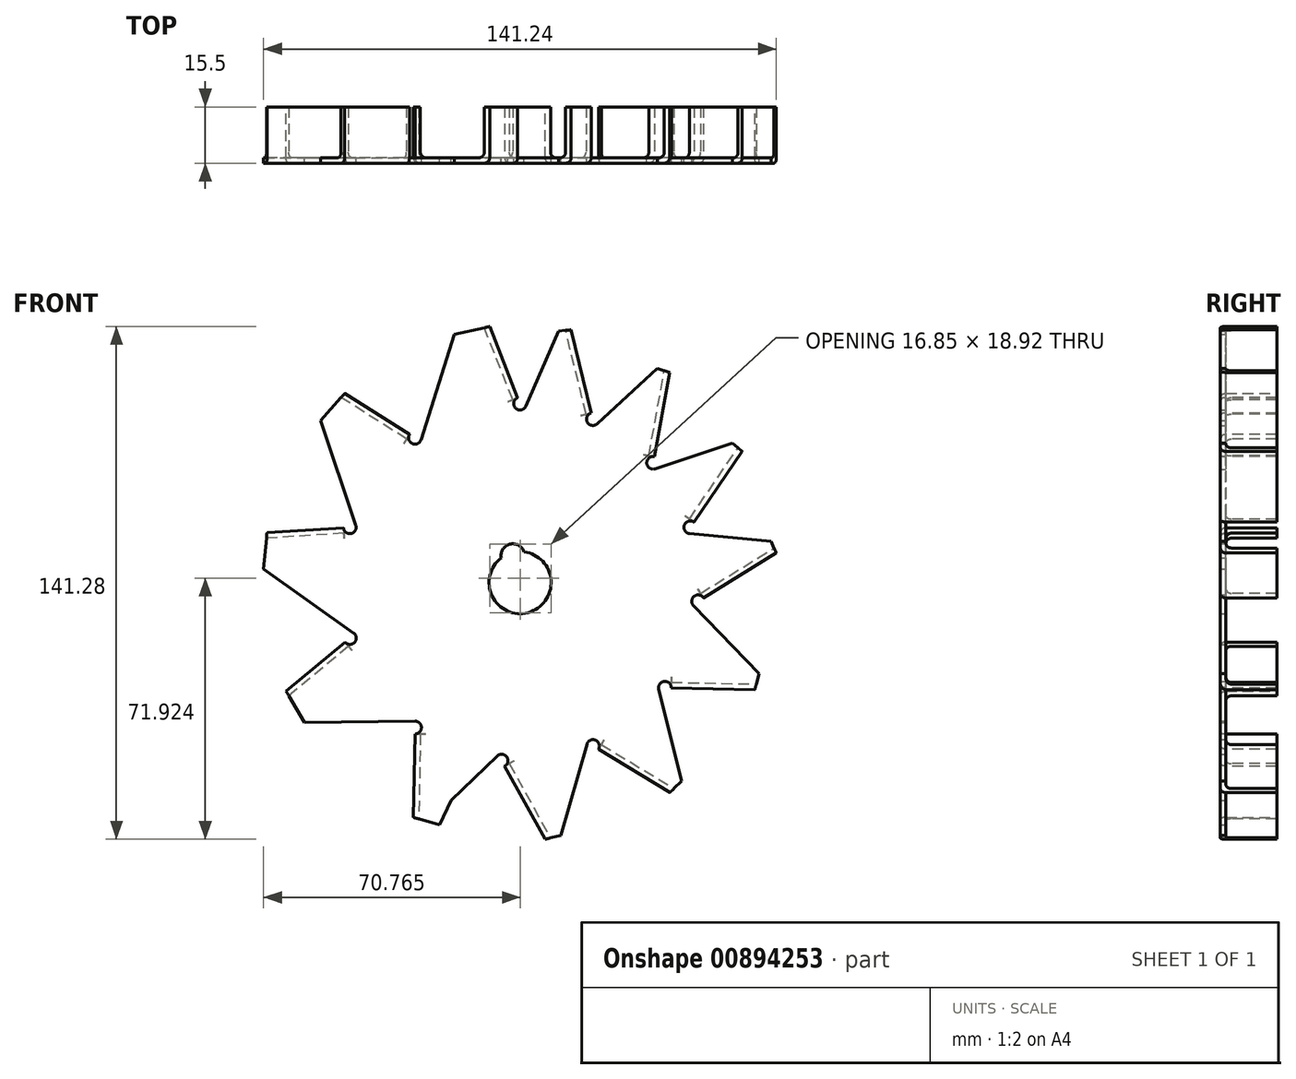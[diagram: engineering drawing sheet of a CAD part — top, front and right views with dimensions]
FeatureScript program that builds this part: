
annotation { "Feature Type Name" : "Feature", "Feature Type Description" : "" }
export const myFeature = defineFeature(function(context is Context, id is Id, definition is map)
    precondition{}
    {
        {
            var Q0;
            Q0=qCreatedBy(makeId("Front.planeOp"),FACE);
            var sketch = newSketch(context, id + "F0", { "sketchPlane" : qUnion([Q0])});
            skArc(sketch, "E0", {"start": v(-5.18, 6.8) * mm, "mid": v(2.21, -8.26) * mm, "end": v(1.09, 8.48) * mm});
            skArc(sketch, "E1", {"start": v(-0.64, 50.93) * mm, "mid": v(-1.26, 48.08) * mm, "end": v(1.6, 48.6) * mm});
            skArc(sketch, "E2", {"start": v(19.64, 46.74) * mm, "mid": v(18.5, 44.21) * mm, "end": v(21.23, 43.75) * mm});
            skArc(sketch, "E3", {"start": v(36.95, 34.71) * mm, "mid": v(34.9, 32.86) * mm, "end": v(37.2, 31.33) * mm});
            skArc(sketch, "E4", {"start": v(47.87, 16.68) * mm, "mid": v(45.24, 15.83) * mm, "end": v(46.72, 13.5) * mm});
            skArc(sketch, "E5", {"start": v(50.52, -4.23) * mm, "mid": v(47.96, -3.77) * mm, "end": v(47.77, -6.37) * mm});
            skArc(sketch, "E6", {"start": v(41.65, -29) * mm, "mid": v(39.7, -27.22) * mm, "end": v(38.2, -29.39) * mm});
            skArc(sketch, "E7", {"start": v(21.59, -45.93) * mm, "mid": v(20.79, -43.42) * mm, "end": v(18.4, -44.54) * mm});
            skArc(sketch, "E8", {"start": v(-4.25, -50.57) * mm, "mid": v(-3.69, -48) * mm, "end": v(-6.3, -47.78) * mm});
            skArc(sketch, "E9", {"start": v(-28.95, -41.68) * mm, "mid": v(-27.16, -39.94) * mm, "end": v(-28.93, -38.18) * mm});
            skArc(sketch, "E10", {"start": v(-48.22, -16.4) * mm, "mid": v(-45.59, -16.47) * mm, "end": v(-45.86, -13.86) * mm});
            skArc(sketch, "E11", {"start": v(-48.64, 15.1) * mm, "mid": v(-46.56, 13.5) * mm, "end": v(-45.23, 15.77) * mm});
            skArc(sketch, "E12", {"start": v(-30.44, 40.83) * mm, "mid": v(-29.7, 38.3) * mm, "end": v(-27.3, 39.37) * mm});
            skLineSegment(sketch, "E13", {"start": v(10.58, 69.25) * mm, "end": v(1.6, 48.6) * mm});
            skLineSegment(sketch, "E14", {"start": v(37.83, 58.96) * mm, "end": v(21.23, 43.75) * mm});
            skLineSegment(sketch, "E15", {"start": v(58.54, 38.47) * mm, "end": v(37.2, 31.33) * mm});
            skLineSegment(sketch, "E16", {"start": v(69.13, 11.34) * mm, "end": v(46.72, 13.5) * mm});
            skLineSegment(sketch, "E17", {"start": v(-18.13, 68.4) * mm, "end": v(-27.3, 39.37) * mm});
            skLineSegment(sketch, "E18", {"start": v(-54.9, 44.64) * mm, "end": v(-45.23, 15.77) * mm});
            skLineSegment(sketch, "E19", {"start": v(-70.66, 3.8) * mm, "end": v(-45.86, -13.86) * mm});
            skLineSegment(sketch, "E20", {"start": v(-59.37, -38.5) * mm, "end": v(-28.93, -38.18) * mm});
            skLineSegment(sketch, "E21", {"start": v(-18.96, -60.03) * mm, "end": v(-6.3, -47.78) * mm});
            skLineSegment(sketch, "E22", {"start": v(11.24, -69.62) * mm, "end": v(18.4, -44.54) * mm});
            skLineSegment(sketch, "E23", {"start": v(44.52, -54.7) * mm, "end": v(38.2, -29.39) * mm});
            skLineSegment(sketch, "E24", {"start": v(65.9, -25.14) * mm, "end": v(47.77, -6.37) * mm});
            skLineSegment(sketch, "E25", {"start": v(10.58, 69.25) * mm, "end": v(14.06, 69.64) * mm});
            skLineSegment(sketch, "E26", {"start": v(37.83, 58.96) * mm, "end": v(41.17, 57.9) * mm});
            skLineSegment(sketch, "E27", {"start": v(58.54, 38.47) * mm, "end": v(61.16, 36.15) * mm});
            skLineSegment(sketch, "E28", {"start": v(69.13, 11.34) * mm, "end": v(70.58, 8.15) * mm});
            skLineSegment(sketch, "E29", {"start": v(14.06, 69.64) * mm, "end": v(19.64, 46.74) * mm});
            skLineSegment(sketch, "E30", {"start": v(41.17, 57.9) * mm, "end": v(36.95, 34.71) * mm});
            skLineSegment(sketch, "E31", {"start": v(61.16, 36.15) * mm, "end": v(47.87, 16.68) * mm});
            skLineSegment(sketch, "E32", {"start": v(70.58, 8.15) * mm, "end": v(50.52, -4.23) * mm});
            skLineSegment(sketch, "E33", {"start": v(65.9, -25.14) * mm, "end": v(64.65, -29.46) * mm});
            skLineSegment(sketch, "E34", {"start": v(64.65, -29.46) * mm, "end": v(41.65, -29) * mm});
            skLineSegment(sketch, "E35", {"start": v(44.52, -54.7) * mm, "end": v(41.29, -57.82) * mm});
            skLineSegment(sketch, "E36", {"start": v(41.29, -57.82) * mm, "end": v(21.59, -45.93) * mm});
            skLineSegment(sketch, "E37", {"start": v(6.87, -70.72) * mm, "end": v(-4.25, -50.57) * mm});
            skLineSegment(sketch, "E38", {"start": v(-29.38, -64.7) * mm, "end": v(-28.95, -41.68) * mm});
            skLineSegment(sketch, "E39", {"start": v(6.87, -70.72) * mm, "end": v(11.24, -69.62) * mm});
            skLineSegment(sketch, "E40", {"start": v(-29.38, -64.7) * mm, "end": v(-22.17, -66.75) * mm});
            skLineSegment(sketch, "E41", {"start": v(-22.17, -66.75) * mm, "end": v(-18.96, -60.03) * mm});
            skLineSegment(sketch, "E42", {"start": v(-59.37, -38.5) * mm, "end": v(-64.46, -29.9) * mm});
            skLineSegment(sketch, "E43", {"start": v(-64.46, -29.9) * mm, "end": v(-48.22, -16.4) * mm});
            skLineSegment(sketch, "E44", {"start": v(-70.66, 3.8) * mm, "end": v(-69.7, 13.75) * mm});
            skLineSegment(sketch, "E45", {"start": v(-69.7, 13.75) * mm, "end": v(-48.64, 15.1) * mm});
            skLineSegment(sketch, "E46", {"start": v(-54.9, 44.64) * mm, "end": v(-48.28, 52.13) * mm});
            skLineSegment(sketch, "E47", {"start": v(-48.28, 52.13) * mm, "end": v(-30.44, 40.83) * mm});
            skLineSegment(sketch, "E48", {"start": v(-18.13, 68.4) * mm, "end": v(-8.37, 70.56) * mm});
            skLineSegment(sketch, "E49", {"start": v(-8.37, 70.56) * mm, "end": v(-0.64, 50.93) * mm});
            skArc(sketch, "E50", {"start": v(1.09, 8.48) * mm, "mid": v(-2.83, 10.58) * mm, "end": v(-5.18, 6.8) * mm});
            skLineSegment(sketch, "E51", {"start": v(-4.79, 40.08) * mm, "end": v(-9.77, 40.51) * mm});
            skLineSegment(sketch, "E52", {"start": v(-15.9, 37.1) * mm, "end": v(-7.2, 39.43) * mm});
            skLineSegment(sketch, "E53", {"start": v(-4.79, 40.08) * mm, "end": v(-8.88, 37.2) * mm});
            skSolve(sketch);
        }
        {
            var Q0;
            Q0 = qSketchRegion(id + "F0", true);
            extrude(context, id + "F1", {"entities" : qUnion([Q0]), "depth" : 1.5 * mm, "offsetDistance" : 25 * mm});
        }
        {
            var Q0;
            Q0=makeQuery(id+"F1.opExtrude","CAP_FACE",FACE,{"disambiguationData":[OSD([sQuery(id+"F0.wireOp",EDGE,"E0"),sQuery(id+"F0.wireOp",EDGE,"E1"),sQuery(id+"F0.wireOp",EDGE,"E2"),sQuery(id+"F0.wireOp",EDGE,"E3"),sQuery(id+"F0.wireOp",EDGE,"E4"),sQuery(id+"F0.wireOp",EDGE,"E5"),sQuery(id+"F0.wireOp",EDGE,"E6"),sQuery(id+"F0.wireOp",EDGE,"E7"),sQuery(id+"F0.wireOp",EDGE,"E8"),sQuery(id+"F0.wireOp",EDGE,"E9"),sQuery(id+"F0.wireOp",EDGE,"E10"),sQuery(id+"F0.wireOp",EDGE,"E11"),sQuery(id+"F0.wireOp",EDGE,"E12"),sQuery(id+"F0.wireOp",EDGE,"E13"),sQuery(id+"F0.wireOp",EDGE,"E14"),sQuery(id+"F0.wireOp",EDGE,"E15"),sQuery(id+"F0.wireOp",EDGE,"E16"),sQuery(id+"F0.wireOp",EDGE,"E17"),sQuery(id+"F0.wireOp",EDGE,"E18"),sQuery(id+"F0.wireOp",EDGE,"E19"),sQuery(id+"F0.wireOp",EDGE,"E20"),sQuery(id+"F0.wireOp",EDGE,"E21"),sQuery(id+"F0.wireOp",EDGE,"E22"),sQuery(id+"F0.wireOp",EDGE,"E23"),sQuery(id+"F0.wireOp",EDGE,"E24"),sQuery(id+"F0.wireOp",EDGE,"E25"),sQuery(id+"F0.wireOp",EDGE,"E26"),sQuery(id+"F0.wireOp",EDGE,"E27"),sQuery(id+"F0.wireOp",EDGE,"E28"),sQuery(id+"F0.wireOp",EDGE,"E29"),sQuery(id+"F0.wireOp",EDGE,"E30"),sQuery(id+"F0.wireOp",EDGE,"E31"),sQuery(id+"F0.wireOp",EDGE,"E32"),sQuery(id+"F0.wireOp",EDGE,"E33"),sQuery(id+"F0.wireOp",EDGE,"E34"),sQuery(id+"F0.wireOp",EDGE,"E35"),sQuery(id+"F0.wireOp",EDGE,"E36"),sQuery(id+"F0.wireOp",EDGE,"E37"),sQuery(id+"F0.wireOp",EDGE,"E38"),sQuery(id+"F0.wireOp",EDGE,"E39"),sQuery(id+"F0.wireOp",EDGE,"E40"),sQuery(id+"F0.wireOp",EDGE,"E41"),sQuery(id+"F0.wireOp",EDGE,"E42"),sQuery(id+"F0.wireOp",EDGE,"E43"),sQuery(id+"F0.wireOp",EDGE,"E44"),sQuery(id+"F0.wireOp",EDGE,"E45"),sQuery(id+"F0.wireOp",EDGE,"E46"),sQuery(id+"F0.wireOp",EDGE,"E47"),sQuery(id+"F0.wireOp",EDGE,"E48"),sQuery(id+"F0.wireOp",EDGE,"E49"),sQuery(id+"F0.wireOp",EDGE,"E50")])],"isStart":false});
            var sketch = newSketch(context, id + "F2", { "sketchPlane" : qUnion([Q0])});
            skLineSegment(sketch, "E54.0", {"start": v(-48.28, 52.13) * mm, "end": v(-30.44, 40.83) * mm});
            skLineSegment(sketch, "E55.0", {"start": v(-8.37, 70.56) * mm, "end": v(-0.64, 50.93) * mm});
            skLineSegment(sketch, "E56.0", {"start": v(14.06, 69.64) * mm, "end": v(19.64, 46.74) * mm});
            skLineSegment(sketch, "E57.0", {"start": v(41.17, 57.9) * mm, "end": v(36.95, 34.71) * mm});
            skLineSegment(sketch, "E58.0", {"start": v(61.16, 36.15) * mm, "end": v(47.87, 16.68) * mm});
            skLineSegment(sketch, "E59.0", {"start": v(70.58, 8.15) * mm, "end": v(50.52, -4.23) * mm});
            skLineSegment(sketch, "E60.0", {"start": v(64.65, -29.46) * mm, "end": v(41.65, -29) * mm});
            skLineSegment(sketch, "E61.0", {"start": v(41.29, -57.82) * mm, "end": v(21.59, -45.93) * mm});
            skLineSegment(sketch, "E62.0", {"start": v(6.87, -70.72) * mm, "end": v(-4.25, -50.57) * mm});
            skLineSegment(sketch, "E63.0", {"start": v(-29.38, -64.7) * mm, "end": v(-28.95, -41.68) * mm});
            skLineSegment(sketch, "E64.0", {"start": v(-64.46, -29.9) * mm, "end": v(-48.22, -16.4) * mm});
            skLineSegment(sketch, "E65.0", {"start": v(-69.7, 13.75) * mm, "end": v(-48.64, 15.1) * mm});
            skLineSegment(sketch, "E66", {"start": v(-30.44, 40.83) * mm, "end": v(-31.25, 39.56) * mm});
            skLineSegment(sketch, "E67", {"start": v(-31.25, 39.56) * mm, "end": v(-49.28, 51) * mm});
            skLineSegment(sketch, "E68", {"start": v(-0.64, 50.93) * mm, "end": v(-2.04, 50.38) * mm});
            skLineSegment(sketch, "E69", {"start": v(-2.04, 50.38) * mm, "end": v(-9.85, 70.23) * mm});
            skLineSegment(sketch, "E70", {"start": v(19.64, 46.74) * mm, "end": v(18.18, 46.38) * mm});
            skLineSegment(sketch, "E71", {"start": v(18.18, 46.38) * mm, "end": v(12.56, 69.47) * mm});
            skLineSegment(sketch, "E72", {"start": v(36.95, 34.71) * mm, "end": v(35.47, 34.98) * mm});
            skLineSegment(sketch, "E73", {"start": v(35.47, 34.98) * mm, "end": v(39.73, 58.36) * mm});
            skLineSegment(sketch, "E74", {"start": v(47.87, 16.68) * mm, "end": v(46.63, 17.53) * mm});
            skLineSegment(sketch, "E75", {"start": v(46.63, 17.53) * mm, "end": v(60.03, 37.16) * mm});
            skLineSegment(sketch, "E76", {"start": v(50.52, -4.23) * mm, "end": v(49.73, -2.96) * mm});
            skLineSegment(sketch, "E77", {"start": v(49.73, -2.96) * mm, "end": v(69.95, 9.53) * mm});
            skLineSegment(sketch, "E78", {"start": v(41.65, -29) * mm, "end": v(41.68, -27.5) * mm});
            skLineSegment(sketch, "E79", {"start": v(41.68, -27.5) * mm, "end": v(65.08, -27.97) * mm});
            skLineSegment(sketch, "E80", {"start": v(21.59, -45.93) * mm, "end": v(22.36, -44.64) * mm});
            skLineSegment(sketch, "E81", {"start": v(22.36, -44.64) * mm, "end": v(42.4, -56.75) * mm});
            skLineSegment(sketch, "E82", {"start": v(-4.25, -50.57) * mm, "end": v(-2.93, -49.84) * mm});
            skLineSegment(sketch, "E83", {"start": v(-2.93, -49.84) * mm, "end": v(8.38, -70.34) * mm});
            skLineSegment(sketch, "E84", {"start": v(6.87, -70.72) * mm, "end": v(8.38, -70.34) * mm});
            skLineSegment(sketch, "E85", {"start": v(41.29, -57.82) * mm, "end": v(42.4, -56.75) * mm});
            skLineSegment(sketch, "E86", {"start": v(64.65, -29.46) * mm, "end": v(65.08, -27.97) * mm});
            skLineSegment(sketch, "E87", {"start": v(70.58, 8.15) * mm, "end": v(69.95, 9.53) * mm});
            skLineSegment(sketch, "E88", {"start": v(61.16, 36.15) * mm, "end": v(60.03, 37.16) * mm});
            skLineSegment(sketch, "E89", {"start": v(41.17, 57.9) * mm, "end": v(39.73, 58.36) * mm});
            skLineSegment(sketch, "E90", {"start": v(14.06, 69.64) * mm, "end": v(12.56, 69.47) * mm});
            skLineSegment(sketch, "E91", {"start": v(-8.37, 70.56) * mm, "end": v(-9.85, 70.23) * mm});
            skLineSegment(sketch, "E92", {"start": v(-48.28, 52.13) * mm, "end": v(-49.28, 51) * mm});
            skLineSegment(sketch, "E93", {"start": v(-48.64, 15.1) * mm, "end": v(-48.54, 13.6) * mm});
            skLineSegment(sketch, "E94", {"start": v(-48.54, 13.6) * mm, "end": v(-69.85, 12.24) * mm});
            skLineSegment(sketch, "E95", {"start": v(-69.85, 12.24) * mm, "end": v(-69.7, 13.75) * mm});
            skLineSegment(sketch, "E96", {"start": v(-28.95, -41.68) * mm, "end": v(-27.45, -41.71) * mm});
            skLineSegment(sketch, "E97", {"start": v(-27.45, -41.71) * mm, "end": v(-27.89, -65.12) * mm});
            skLineSegment(sketch, "E98", {"start": v(-27.89, -65.12) * mm, "end": v(-29.38, -64.7) * mm});
            skLineSegment(sketch, "E99", {"start": v(-48.22, -16.4) * mm, "end": v(-47.26, -17.55) * mm});
            skLineSegment(sketch, "E100", {"start": v(-47.26, -17.55) * mm, "end": v(-63.68, -31.2) * mm});
            skLineSegment(sketch, "E101", {"start": v(-64.46, -29.9) * mm, "end": v(-63.68, -31.2) * mm});
            skSolve(sketch);
        }
        {
            var Q0;
            Q0 = qSketchRegion(id + "F2", true);
            extrude(context, id + "F3", {"entities" : qUnion([Q0]), "operationType" : NewBodyOperationType.ADD, "oppositeDirection" : true, "depth" : 15.5 * mm, "offsetDistance" : 25 * mm});
        }
        {
            var Q0;
            Q0=makeQuery(id+"F3.boolean.opBoolean","INTERSECT",EDGE,{"derivedFrom":[makeQuery(id+"F1.opExtrude","CAP_FACE",FACE,{"disambiguationData":[OSD([sQuery(id+"F0.wireOp",EDGE,"E0"),sQuery(id+"F0.wireOp",EDGE,"E1"),sQuery(id+"F0.wireOp",EDGE,"E2"),sQuery(id+"F0.wireOp",EDGE,"E3"),sQuery(id+"F0.wireOp",EDGE,"E4"),sQuery(id+"F0.wireOp",EDGE,"E5"),sQuery(id+"F0.wireOp",EDGE,"E6"),sQuery(id+"F0.wireOp",EDGE,"E7"),sQuery(id+"F0.wireOp",EDGE,"E8"),sQuery(id+"F0.wireOp",EDGE,"E9"),sQuery(id+"F0.wireOp",EDGE,"E10"),sQuery(id+"F0.wireOp",EDGE,"E11"),sQuery(id+"F0.wireOp",EDGE,"E12"),sQuery(id+"F0.wireOp",EDGE,"E13"),sQuery(id+"F0.wireOp",EDGE,"E14"),sQuery(id+"F0.wireOp",EDGE,"E15"),sQuery(id+"F0.wireOp",EDGE,"E16"),sQuery(id+"F0.wireOp",EDGE,"E17"),sQuery(id+"F0.wireOp",EDGE,"E18"),sQuery(id+"F0.wireOp",EDGE,"E19"),sQuery(id+"F0.wireOp",EDGE,"E20"),sQuery(id+"F0.wireOp",EDGE,"E21"),sQuery(id+"F0.wireOp",EDGE,"E22"),sQuery(id+"F0.wireOp",EDGE,"E23"),sQuery(id+"F0.wireOp",EDGE,"E24"),sQuery(id+"F0.wireOp",EDGE,"E25"),sQuery(id+"F0.wireOp",EDGE,"E26"),sQuery(id+"F0.wireOp",EDGE,"E27"),sQuery(id+"F0.wireOp",EDGE,"E28"),sQuery(id+"F0.wireOp",EDGE,"E29"),sQuery(id+"F0.wireOp",EDGE,"E30"),sQuery(id+"F0.wireOp",EDGE,"E31"),sQuery(id+"F0.wireOp",EDGE,"E32"),sQuery(id+"F0.wireOp",EDGE,"E33"),sQuery(id+"F0.wireOp",EDGE,"E34"),sQuery(id+"F0.wireOp",EDGE,"E35"),sQuery(id+"F0.wireOp",EDGE,"E36"),sQuery(id+"F0.wireOp",EDGE,"E37"),sQuery(id+"F0.wireOp",EDGE,"E38"),sQuery(id+"F0.wireOp",EDGE,"E39"),sQuery(id+"F0.wireOp",EDGE,"E40"),sQuery(id+"F0.wireOp",EDGE,"E41"),sQuery(id+"F0.wireOp",EDGE,"E42"),sQuery(id+"F0.wireOp",EDGE,"E43"),sQuery(id+"F0.wireOp",EDGE,"E44"),sQuery(id+"F0.wireOp",EDGE,"E45"),sQuery(id+"F0.wireOp",EDGE,"E46"),sQuery(id+"F0.wireOp",EDGE,"E47"),sQuery(id+"F0.wireOp",EDGE,"E48"),sQuery(id+"F0.wireOp",EDGE,"E49"),sQuery(id+"F0.wireOp",EDGE,"E50")])],"isStart":true}),makeQuery(id+"F3.opExtrude","SWEPT_FACE",FACE,{"disambiguationData":[OSD([sQuery(id+"F2.wireOp",EDGE,"E69")])]})]});
            var Q1;
            Q1=makeQuery(id+"F3.boolean.opBoolean","INTERSECT",EDGE,{"derivedFrom":[makeQuery(id+"F1.opExtrude","CAP_FACE",FACE,{"disambiguationData":[OSD([sQuery(id+"F0.wireOp",EDGE,"E0"),sQuery(id+"F0.wireOp",EDGE,"E1"),sQuery(id+"F0.wireOp",EDGE,"E2"),sQuery(id+"F0.wireOp",EDGE,"E3"),sQuery(id+"F0.wireOp",EDGE,"E4"),sQuery(id+"F0.wireOp",EDGE,"E5"),sQuery(id+"F0.wireOp",EDGE,"E6"),sQuery(id+"F0.wireOp",EDGE,"E7"),sQuery(id+"F0.wireOp",EDGE,"E8"),sQuery(id+"F0.wireOp",EDGE,"E9"),sQuery(id+"F0.wireOp",EDGE,"E10"),sQuery(id+"F0.wireOp",EDGE,"E11"),sQuery(id+"F0.wireOp",EDGE,"E12"),sQuery(id+"F0.wireOp",EDGE,"E13"),sQuery(id+"F0.wireOp",EDGE,"E14"),sQuery(id+"F0.wireOp",EDGE,"E15"),sQuery(id+"F0.wireOp",EDGE,"E16"),sQuery(id+"F0.wireOp",EDGE,"E17"),sQuery(id+"F0.wireOp",EDGE,"E18"),sQuery(id+"F0.wireOp",EDGE,"E19"),sQuery(id+"F0.wireOp",EDGE,"E20"),sQuery(id+"F0.wireOp",EDGE,"E21"),sQuery(id+"F0.wireOp",EDGE,"E22"),sQuery(id+"F0.wireOp",EDGE,"E23"),sQuery(id+"F0.wireOp",EDGE,"E24"),sQuery(id+"F0.wireOp",EDGE,"E25"),sQuery(id+"F0.wireOp",EDGE,"E26"),sQuery(id+"F0.wireOp",EDGE,"E27"),sQuery(id+"F0.wireOp",EDGE,"E28"),sQuery(id+"F0.wireOp",EDGE,"E29"),sQuery(id+"F0.wireOp",EDGE,"E30"),sQuery(id+"F0.wireOp",EDGE,"E31"),sQuery(id+"F0.wireOp",EDGE,"E32"),sQuery(id+"F0.wireOp",EDGE,"E33"),sQuery(id+"F0.wireOp",EDGE,"E34"),sQuery(id+"F0.wireOp",EDGE,"E35"),sQuery(id+"F0.wireOp",EDGE,"E36"),sQuery(id+"F0.wireOp",EDGE,"E37"),sQuery(id+"F0.wireOp",EDGE,"E38"),sQuery(id+"F0.wireOp",EDGE,"E39"),sQuery(id+"F0.wireOp",EDGE,"E40"),sQuery(id+"F0.wireOp",EDGE,"E41"),sQuery(id+"F0.wireOp",EDGE,"E42"),sQuery(id+"F0.wireOp",EDGE,"E43"),sQuery(id+"F0.wireOp",EDGE,"E44"),sQuery(id+"F0.wireOp",EDGE,"E45"),sQuery(id+"F0.wireOp",EDGE,"E46"),sQuery(id+"F0.wireOp",EDGE,"E47"),sQuery(id+"F0.wireOp",EDGE,"E48"),sQuery(id+"F0.wireOp",EDGE,"E49"),sQuery(id+"F0.wireOp",EDGE,"E50")])],"isStart":true}),makeQuery(id+"F3.opExtrude","SWEPT_FACE",FACE,{"disambiguationData":[OSD([sQuery(id+"F2.wireOp",EDGE,"E67")])]})]});
            var Q2;
            Q2=makeQuery(id+"F3.boolean.opBoolean","INTERSECT",EDGE,{"derivedFrom":[makeQuery(id+"F1.opExtrude","CAP_FACE",FACE,{"disambiguationData":[OSD([sQuery(id+"F0.wireOp",EDGE,"E0"),sQuery(id+"F0.wireOp",EDGE,"E1"),sQuery(id+"F0.wireOp",EDGE,"E2"),sQuery(id+"F0.wireOp",EDGE,"E3"),sQuery(id+"F0.wireOp",EDGE,"E4"),sQuery(id+"F0.wireOp",EDGE,"E5"),sQuery(id+"F0.wireOp",EDGE,"E6"),sQuery(id+"F0.wireOp",EDGE,"E7"),sQuery(id+"F0.wireOp",EDGE,"E8"),sQuery(id+"F0.wireOp",EDGE,"E9"),sQuery(id+"F0.wireOp",EDGE,"E10"),sQuery(id+"F0.wireOp",EDGE,"E11"),sQuery(id+"F0.wireOp",EDGE,"E12"),sQuery(id+"F0.wireOp",EDGE,"E13"),sQuery(id+"F0.wireOp",EDGE,"E14"),sQuery(id+"F0.wireOp",EDGE,"E15"),sQuery(id+"F0.wireOp",EDGE,"E16"),sQuery(id+"F0.wireOp",EDGE,"E17"),sQuery(id+"F0.wireOp",EDGE,"E18"),sQuery(id+"F0.wireOp",EDGE,"E19"),sQuery(id+"F0.wireOp",EDGE,"E20"),sQuery(id+"F0.wireOp",EDGE,"E21"),sQuery(id+"F0.wireOp",EDGE,"E22"),sQuery(id+"F0.wireOp",EDGE,"E23"),sQuery(id+"F0.wireOp",EDGE,"E24"),sQuery(id+"F0.wireOp",EDGE,"E25"),sQuery(id+"F0.wireOp",EDGE,"E26"),sQuery(id+"F0.wireOp",EDGE,"E27"),sQuery(id+"F0.wireOp",EDGE,"E28"),sQuery(id+"F0.wireOp",EDGE,"E29"),sQuery(id+"F0.wireOp",EDGE,"E30"),sQuery(id+"F0.wireOp",EDGE,"E31"),sQuery(id+"F0.wireOp",EDGE,"E32"),sQuery(id+"F0.wireOp",EDGE,"E33"),sQuery(id+"F0.wireOp",EDGE,"E34"),sQuery(id+"F0.wireOp",EDGE,"E35"),sQuery(id+"F0.wireOp",EDGE,"E36"),sQuery(id+"F0.wireOp",EDGE,"E37"),sQuery(id+"F0.wireOp",EDGE,"E38"),sQuery(id+"F0.wireOp",EDGE,"E39"),sQuery(id+"F0.wireOp",EDGE,"E40"),sQuery(id+"F0.wireOp",EDGE,"E41"),sQuery(id+"F0.wireOp",EDGE,"E42"),sQuery(id+"F0.wireOp",EDGE,"E43"),sQuery(id+"F0.wireOp",EDGE,"E44"),sQuery(id+"F0.wireOp",EDGE,"E45"),sQuery(id+"F0.wireOp",EDGE,"E46"),sQuery(id+"F0.wireOp",EDGE,"E47"),sQuery(id+"F0.wireOp",EDGE,"E48"),sQuery(id+"F0.wireOp",EDGE,"E49"),sQuery(id+"F0.wireOp",EDGE,"E50")])],"isStart":true}),makeQuery(id+"F3.opExtrude","SWEPT_FACE",FACE,{"disambiguationData":[OSD([sQuery(id+"F2.wireOp",EDGE,"E94")])]})]});
            var Q3;
            Q3=makeQuery(id+"F3.boolean.opBoolean","INTERSECT",EDGE,{"derivedFrom":[makeQuery(id+"F1.opExtrude","CAP_FACE",FACE,{"disambiguationData":[OSD([sQuery(id+"F0.wireOp",EDGE,"E0"),sQuery(id+"F0.wireOp",EDGE,"E1"),sQuery(id+"F0.wireOp",EDGE,"E2"),sQuery(id+"F0.wireOp",EDGE,"E3"),sQuery(id+"F0.wireOp",EDGE,"E4"),sQuery(id+"F0.wireOp",EDGE,"E5"),sQuery(id+"F0.wireOp",EDGE,"E6"),sQuery(id+"F0.wireOp",EDGE,"E7"),sQuery(id+"F0.wireOp",EDGE,"E8"),sQuery(id+"F0.wireOp",EDGE,"E9"),sQuery(id+"F0.wireOp",EDGE,"E10"),sQuery(id+"F0.wireOp",EDGE,"E11"),sQuery(id+"F0.wireOp",EDGE,"E12"),sQuery(id+"F0.wireOp",EDGE,"E13"),sQuery(id+"F0.wireOp",EDGE,"E14"),sQuery(id+"F0.wireOp",EDGE,"E15"),sQuery(id+"F0.wireOp",EDGE,"E16"),sQuery(id+"F0.wireOp",EDGE,"E17"),sQuery(id+"F0.wireOp",EDGE,"E18"),sQuery(id+"F0.wireOp",EDGE,"E19"),sQuery(id+"F0.wireOp",EDGE,"E20"),sQuery(id+"F0.wireOp",EDGE,"E21"),sQuery(id+"F0.wireOp",EDGE,"E22"),sQuery(id+"F0.wireOp",EDGE,"E23"),sQuery(id+"F0.wireOp",EDGE,"E24"),sQuery(id+"F0.wireOp",EDGE,"E25"),sQuery(id+"F0.wireOp",EDGE,"E26"),sQuery(id+"F0.wireOp",EDGE,"E27"),sQuery(id+"F0.wireOp",EDGE,"E28"),sQuery(id+"F0.wireOp",EDGE,"E29"),sQuery(id+"F0.wireOp",EDGE,"E30"),sQuery(id+"F0.wireOp",EDGE,"E31"),sQuery(id+"F0.wireOp",EDGE,"E32"),sQuery(id+"F0.wireOp",EDGE,"E33"),sQuery(id+"F0.wireOp",EDGE,"E34"),sQuery(id+"F0.wireOp",EDGE,"E35"),sQuery(id+"F0.wireOp",EDGE,"E36"),sQuery(id+"F0.wireOp",EDGE,"E37"),sQuery(id+"F0.wireOp",EDGE,"E38"),sQuery(id+"F0.wireOp",EDGE,"E39"),sQuery(id+"F0.wireOp",EDGE,"E40"),sQuery(id+"F0.wireOp",EDGE,"E41"),sQuery(id+"F0.wireOp",EDGE,"E42"),sQuery(id+"F0.wireOp",EDGE,"E43"),sQuery(id+"F0.wireOp",EDGE,"E44"),sQuery(id+"F0.wireOp",EDGE,"E45"),sQuery(id+"F0.wireOp",EDGE,"E46"),sQuery(id+"F0.wireOp",EDGE,"E47"),sQuery(id+"F0.wireOp",EDGE,"E48"),sQuery(id+"F0.wireOp",EDGE,"E49"),sQuery(id+"F0.wireOp",EDGE,"E50")])],"isStart":true}),makeQuery(id+"F3.opExtrude","SWEPT_FACE",FACE,{"disambiguationData":[OSD([sQuery(id+"F2.wireOp",EDGE,"E100")])]})]});
            var Q4;
            Q4=makeQuery(id+"F3.boolean.opBoolean","INTERSECT",EDGE,{"derivedFrom":[makeQuery(id+"F1.opExtrude","CAP_FACE",FACE,{"disambiguationData":[OSD([sQuery(id+"F0.wireOp",EDGE,"E0"),sQuery(id+"F0.wireOp",EDGE,"E1"),sQuery(id+"F0.wireOp",EDGE,"E2"),sQuery(id+"F0.wireOp",EDGE,"E3"),sQuery(id+"F0.wireOp",EDGE,"E4"),sQuery(id+"F0.wireOp",EDGE,"E5"),sQuery(id+"F0.wireOp",EDGE,"E6"),sQuery(id+"F0.wireOp",EDGE,"E7"),sQuery(id+"F0.wireOp",EDGE,"E8"),sQuery(id+"F0.wireOp",EDGE,"E9"),sQuery(id+"F0.wireOp",EDGE,"E10"),sQuery(id+"F0.wireOp",EDGE,"E11"),sQuery(id+"F0.wireOp",EDGE,"E12"),sQuery(id+"F0.wireOp",EDGE,"E13"),sQuery(id+"F0.wireOp",EDGE,"E14"),sQuery(id+"F0.wireOp",EDGE,"E15"),sQuery(id+"F0.wireOp",EDGE,"E16"),sQuery(id+"F0.wireOp",EDGE,"E17"),sQuery(id+"F0.wireOp",EDGE,"E18"),sQuery(id+"F0.wireOp",EDGE,"E19"),sQuery(id+"F0.wireOp",EDGE,"E20"),sQuery(id+"F0.wireOp",EDGE,"E21"),sQuery(id+"F0.wireOp",EDGE,"E22"),sQuery(id+"F0.wireOp",EDGE,"E23"),sQuery(id+"F0.wireOp",EDGE,"E24"),sQuery(id+"F0.wireOp",EDGE,"E25"),sQuery(id+"F0.wireOp",EDGE,"E26"),sQuery(id+"F0.wireOp",EDGE,"E27"),sQuery(id+"F0.wireOp",EDGE,"E28"),sQuery(id+"F0.wireOp",EDGE,"E29"),sQuery(id+"F0.wireOp",EDGE,"E30"),sQuery(id+"F0.wireOp",EDGE,"E31"),sQuery(id+"F0.wireOp",EDGE,"E32"),sQuery(id+"F0.wireOp",EDGE,"E33"),sQuery(id+"F0.wireOp",EDGE,"E34"),sQuery(id+"F0.wireOp",EDGE,"E35"),sQuery(id+"F0.wireOp",EDGE,"E36"),sQuery(id+"F0.wireOp",EDGE,"E37"),sQuery(id+"F0.wireOp",EDGE,"E38"),sQuery(id+"F0.wireOp",EDGE,"E39"),sQuery(id+"F0.wireOp",EDGE,"E40"),sQuery(id+"F0.wireOp",EDGE,"E41"),sQuery(id+"F0.wireOp",EDGE,"E42"),sQuery(id+"F0.wireOp",EDGE,"E43"),sQuery(id+"F0.wireOp",EDGE,"E44"),sQuery(id+"F0.wireOp",EDGE,"E45"),sQuery(id+"F0.wireOp",EDGE,"E46"),sQuery(id+"F0.wireOp",EDGE,"E47"),sQuery(id+"F0.wireOp",EDGE,"E48"),sQuery(id+"F0.wireOp",EDGE,"E49"),sQuery(id+"F0.wireOp",EDGE,"E50")])],"isStart":true}),makeQuery(id+"F3.opExtrude","SWEPT_FACE",FACE,{"disambiguationData":[OSD([sQuery(id+"F2.wireOp",EDGE,"E97")])]})]});
            var Q5;
            Q5=makeQuery(id+"F3.boolean.opBoolean","INTERSECT",EDGE,{"derivedFrom":[makeQuery(id+"F1.opExtrude","CAP_FACE",FACE,{"disambiguationData":[OSD([sQuery(id+"F0.wireOp",EDGE,"E0"),sQuery(id+"F0.wireOp",EDGE,"E1"),sQuery(id+"F0.wireOp",EDGE,"E2"),sQuery(id+"F0.wireOp",EDGE,"E3"),sQuery(id+"F0.wireOp",EDGE,"E4"),sQuery(id+"F0.wireOp",EDGE,"E5"),sQuery(id+"F0.wireOp",EDGE,"E6"),sQuery(id+"F0.wireOp",EDGE,"E7"),sQuery(id+"F0.wireOp",EDGE,"E8"),sQuery(id+"F0.wireOp",EDGE,"E9"),sQuery(id+"F0.wireOp",EDGE,"E10"),sQuery(id+"F0.wireOp",EDGE,"E11"),sQuery(id+"F0.wireOp",EDGE,"E12"),sQuery(id+"F0.wireOp",EDGE,"E13"),sQuery(id+"F0.wireOp",EDGE,"E14"),sQuery(id+"F0.wireOp",EDGE,"E15"),sQuery(id+"F0.wireOp",EDGE,"E16"),sQuery(id+"F0.wireOp",EDGE,"E17"),sQuery(id+"F0.wireOp",EDGE,"E18"),sQuery(id+"F0.wireOp",EDGE,"E19"),sQuery(id+"F0.wireOp",EDGE,"E20"),sQuery(id+"F0.wireOp",EDGE,"E21"),sQuery(id+"F0.wireOp",EDGE,"E22"),sQuery(id+"F0.wireOp",EDGE,"E23"),sQuery(id+"F0.wireOp",EDGE,"E24"),sQuery(id+"F0.wireOp",EDGE,"E25"),sQuery(id+"F0.wireOp",EDGE,"E26"),sQuery(id+"F0.wireOp",EDGE,"E27"),sQuery(id+"F0.wireOp",EDGE,"E28"),sQuery(id+"F0.wireOp",EDGE,"E29"),sQuery(id+"F0.wireOp",EDGE,"E30"),sQuery(id+"F0.wireOp",EDGE,"E31"),sQuery(id+"F0.wireOp",EDGE,"E32"),sQuery(id+"F0.wireOp",EDGE,"E33"),sQuery(id+"F0.wireOp",EDGE,"E34"),sQuery(id+"F0.wireOp",EDGE,"E35"),sQuery(id+"F0.wireOp",EDGE,"E36"),sQuery(id+"F0.wireOp",EDGE,"E37"),sQuery(id+"F0.wireOp",EDGE,"E38"),sQuery(id+"F0.wireOp",EDGE,"E39"),sQuery(id+"F0.wireOp",EDGE,"E40"),sQuery(id+"F0.wireOp",EDGE,"E41"),sQuery(id+"F0.wireOp",EDGE,"E42"),sQuery(id+"F0.wireOp",EDGE,"E43"),sQuery(id+"F0.wireOp",EDGE,"E44"),sQuery(id+"F0.wireOp",EDGE,"E45"),sQuery(id+"F0.wireOp",EDGE,"E46"),sQuery(id+"F0.wireOp",EDGE,"E47"),sQuery(id+"F0.wireOp",EDGE,"E48"),sQuery(id+"F0.wireOp",EDGE,"E49"),sQuery(id+"F0.wireOp",EDGE,"E50")])],"isStart":true}),makeQuery(id+"F3.opExtrude","SWEPT_FACE",FACE,{"disambiguationData":[OSD([sQuery(id+"F2.wireOp",EDGE,"E83")])]})]});
            var Q6;
            Q6=makeQuery(id+"F3.boolean.opBoolean","INTERSECT",EDGE,{"derivedFrom":[makeQuery(id+"F1.opExtrude","CAP_FACE",FACE,{"disambiguationData":[OSD([sQuery(id+"F0.wireOp",EDGE,"E0"),sQuery(id+"F0.wireOp",EDGE,"E1"),sQuery(id+"F0.wireOp",EDGE,"E2"),sQuery(id+"F0.wireOp",EDGE,"E3"),sQuery(id+"F0.wireOp",EDGE,"E4"),sQuery(id+"F0.wireOp",EDGE,"E5"),sQuery(id+"F0.wireOp",EDGE,"E6"),sQuery(id+"F0.wireOp",EDGE,"E7"),sQuery(id+"F0.wireOp",EDGE,"E8"),sQuery(id+"F0.wireOp",EDGE,"E9"),sQuery(id+"F0.wireOp",EDGE,"E10"),sQuery(id+"F0.wireOp",EDGE,"E11"),sQuery(id+"F0.wireOp",EDGE,"E12"),sQuery(id+"F0.wireOp",EDGE,"E13"),sQuery(id+"F0.wireOp",EDGE,"E14"),sQuery(id+"F0.wireOp",EDGE,"E15"),sQuery(id+"F0.wireOp",EDGE,"E16"),sQuery(id+"F0.wireOp",EDGE,"E17"),sQuery(id+"F0.wireOp",EDGE,"E18"),sQuery(id+"F0.wireOp",EDGE,"E19"),sQuery(id+"F0.wireOp",EDGE,"E20"),sQuery(id+"F0.wireOp",EDGE,"E21"),sQuery(id+"F0.wireOp",EDGE,"E22"),sQuery(id+"F0.wireOp",EDGE,"E23"),sQuery(id+"F0.wireOp",EDGE,"E24"),sQuery(id+"F0.wireOp",EDGE,"E25"),sQuery(id+"F0.wireOp",EDGE,"E26"),sQuery(id+"F0.wireOp",EDGE,"E27"),sQuery(id+"F0.wireOp",EDGE,"E28"),sQuery(id+"F0.wireOp",EDGE,"E29"),sQuery(id+"F0.wireOp",EDGE,"E30"),sQuery(id+"F0.wireOp",EDGE,"E31"),sQuery(id+"F0.wireOp",EDGE,"E32"),sQuery(id+"F0.wireOp",EDGE,"E33"),sQuery(id+"F0.wireOp",EDGE,"E34"),sQuery(id+"F0.wireOp",EDGE,"E35"),sQuery(id+"F0.wireOp",EDGE,"E36"),sQuery(id+"F0.wireOp",EDGE,"E37"),sQuery(id+"F0.wireOp",EDGE,"E38"),sQuery(id+"F0.wireOp",EDGE,"E39"),sQuery(id+"F0.wireOp",EDGE,"E40"),sQuery(id+"F0.wireOp",EDGE,"E41"),sQuery(id+"F0.wireOp",EDGE,"E42"),sQuery(id+"F0.wireOp",EDGE,"E43"),sQuery(id+"F0.wireOp",EDGE,"E44"),sQuery(id+"F0.wireOp",EDGE,"E45"),sQuery(id+"F0.wireOp",EDGE,"E46"),sQuery(id+"F0.wireOp",EDGE,"E47"),sQuery(id+"F0.wireOp",EDGE,"E48"),sQuery(id+"F0.wireOp",EDGE,"E49"),sQuery(id+"F0.wireOp",EDGE,"E50")])],"isStart":true}),makeQuery(id+"F3.opExtrude","SWEPT_FACE",FACE,{"disambiguationData":[OSD([sQuery(id+"F2.wireOp",EDGE,"E81")])]})]});
            var Q7;
            Q7=makeQuery(id+"F3.boolean.opBoolean","INTERSECT",EDGE,{"derivedFrom":[makeQuery(id+"F1.opExtrude","CAP_FACE",FACE,{"disambiguationData":[OSD([sQuery(id+"F0.wireOp",EDGE,"E0"),sQuery(id+"F0.wireOp",EDGE,"E1"),sQuery(id+"F0.wireOp",EDGE,"E2"),sQuery(id+"F0.wireOp",EDGE,"E3"),sQuery(id+"F0.wireOp",EDGE,"E4"),sQuery(id+"F0.wireOp",EDGE,"E5"),sQuery(id+"F0.wireOp",EDGE,"E6"),sQuery(id+"F0.wireOp",EDGE,"E7"),sQuery(id+"F0.wireOp",EDGE,"E8"),sQuery(id+"F0.wireOp",EDGE,"E9"),sQuery(id+"F0.wireOp",EDGE,"E10"),sQuery(id+"F0.wireOp",EDGE,"E11"),sQuery(id+"F0.wireOp",EDGE,"E12"),sQuery(id+"F0.wireOp",EDGE,"E13"),sQuery(id+"F0.wireOp",EDGE,"E14"),sQuery(id+"F0.wireOp",EDGE,"E15"),sQuery(id+"F0.wireOp",EDGE,"E16"),sQuery(id+"F0.wireOp",EDGE,"E17"),sQuery(id+"F0.wireOp",EDGE,"E18"),sQuery(id+"F0.wireOp",EDGE,"E19"),sQuery(id+"F0.wireOp",EDGE,"E20"),sQuery(id+"F0.wireOp",EDGE,"E21"),sQuery(id+"F0.wireOp",EDGE,"E22"),sQuery(id+"F0.wireOp",EDGE,"E23"),sQuery(id+"F0.wireOp",EDGE,"E24"),sQuery(id+"F0.wireOp",EDGE,"E25"),sQuery(id+"F0.wireOp",EDGE,"E26"),sQuery(id+"F0.wireOp",EDGE,"E27"),sQuery(id+"F0.wireOp",EDGE,"E28"),sQuery(id+"F0.wireOp",EDGE,"E29"),sQuery(id+"F0.wireOp",EDGE,"E30"),sQuery(id+"F0.wireOp",EDGE,"E31"),sQuery(id+"F0.wireOp",EDGE,"E32"),sQuery(id+"F0.wireOp",EDGE,"E33"),sQuery(id+"F0.wireOp",EDGE,"E34"),sQuery(id+"F0.wireOp",EDGE,"E35"),sQuery(id+"F0.wireOp",EDGE,"E36"),sQuery(id+"F0.wireOp",EDGE,"E37"),sQuery(id+"F0.wireOp",EDGE,"E38"),sQuery(id+"F0.wireOp",EDGE,"E39"),sQuery(id+"F0.wireOp",EDGE,"E40"),sQuery(id+"F0.wireOp",EDGE,"E41"),sQuery(id+"F0.wireOp",EDGE,"E42"),sQuery(id+"F0.wireOp",EDGE,"E43"),sQuery(id+"F0.wireOp",EDGE,"E44"),sQuery(id+"F0.wireOp",EDGE,"E45"),sQuery(id+"F0.wireOp",EDGE,"E46"),sQuery(id+"F0.wireOp",EDGE,"E47"),sQuery(id+"F0.wireOp",EDGE,"E48"),sQuery(id+"F0.wireOp",EDGE,"E49"),sQuery(id+"F0.wireOp",EDGE,"E50")])],"isStart":true}),makeQuery(id+"F3.opExtrude","SWEPT_FACE",FACE,{"disambiguationData":[OSD([sQuery(id+"F2.wireOp",EDGE,"E79")])]})]});
            var Q8;
            Q8=makeQuery(id+"F3.boolean.opBoolean","INTERSECT",EDGE,{"derivedFrom":[makeQuery(id+"F1.opExtrude","CAP_FACE",FACE,{"disambiguationData":[OSD([sQuery(id+"F0.wireOp",EDGE,"E0"),sQuery(id+"F0.wireOp",EDGE,"E1"),sQuery(id+"F0.wireOp",EDGE,"E2"),sQuery(id+"F0.wireOp",EDGE,"E3"),sQuery(id+"F0.wireOp",EDGE,"E4"),sQuery(id+"F0.wireOp",EDGE,"E5"),sQuery(id+"F0.wireOp",EDGE,"E6"),sQuery(id+"F0.wireOp",EDGE,"E7"),sQuery(id+"F0.wireOp",EDGE,"E8"),sQuery(id+"F0.wireOp",EDGE,"E9"),sQuery(id+"F0.wireOp",EDGE,"E10"),sQuery(id+"F0.wireOp",EDGE,"E11"),sQuery(id+"F0.wireOp",EDGE,"E12"),sQuery(id+"F0.wireOp",EDGE,"E13"),sQuery(id+"F0.wireOp",EDGE,"E14"),sQuery(id+"F0.wireOp",EDGE,"E15"),sQuery(id+"F0.wireOp",EDGE,"E16"),sQuery(id+"F0.wireOp",EDGE,"E17"),sQuery(id+"F0.wireOp",EDGE,"E18"),sQuery(id+"F0.wireOp",EDGE,"E19"),sQuery(id+"F0.wireOp",EDGE,"E20"),sQuery(id+"F0.wireOp",EDGE,"E21"),sQuery(id+"F0.wireOp",EDGE,"E22"),sQuery(id+"F0.wireOp",EDGE,"E23"),sQuery(id+"F0.wireOp",EDGE,"E24"),sQuery(id+"F0.wireOp",EDGE,"E25"),sQuery(id+"F0.wireOp",EDGE,"E26"),sQuery(id+"F0.wireOp",EDGE,"E27"),sQuery(id+"F0.wireOp",EDGE,"E28"),sQuery(id+"F0.wireOp",EDGE,"E29"),sQuery(id+"F0.wireOp",EDGE,"E30"),sQuery(id+"F0.wireOp",EDGE,"E31"),sQuery(id+"F0.wireOp",EDGE,"E32"),sQuery(id+"F0.wireOp",EDGE,"E33"),sQuery(id+"F0.wireOp",EDGE,"E34"),sQuery(id+"F0.wireOp",EDGE,"E35"),sQuery(id+"F0.wireOp",EDGE,"E36"),sQuery(id+"F0.wireOp",EDGE,"E37"),sQuery(id+"F0.wireOp",EDGE,"E38"),sQuery(id+"F0.wireOp",EDGE,"E39"),sQuery(id+"F0.wireOp",EDGE,"E40"),sQuery(id+"F0.wireOp",EDGE,"E41"),sQuery(id+"F0.wireOp",EDGE,"E42"),sQuery(id+"F0.wireOp",EDGE,"E43"),sQuery(id+"F0.wireOp",EDGE,"E44"),sQuery(id+"F0.wireOp",EDGE,"E45"),sQuery(id+"F0.wireOp",EDGE,"E46"),sQuery(id+"F0.wireOp",EDGE,"E47"),sQuery(id+"F0.wireOp",EDGE,"E48"),sQuery(id+"F0.wireOp",EDGE,"E49"),sQuery(id+"F0.wireOp",EDGE,"E50")])],"isStart":true}),makeQuery(id+"F3.opExtrude","SWEPT_FACE",FACE,{"disambiguationData":[OSD([sQuery(id+"F2.wireOp",EDGE,"E77")])]})]});
            var Q9;
            Q9=makeQuery(id+"F3.boolean.opBoolean","INTERSECT",EDGE,{"derivedFrom":[makeQuery(id+"F1.opExtrude","CAP_FACE",FACE,{"disambiguationData":[OSD([sQuery(id+"F0.wireOp",EDGE,"E0"),sQuery(id+"F0.wireOp",EDGE,"E1"),sQuery(id+"F0.wireOp",EDGE,"E2"),sQuery(id+"F0.wireOp",EDGE,"E3"),sQuery(id+"F0.wireOp",EDGE,"E4"),sQuery(id+"F0.wireOp",EDGE,"E5"),sQuery(id+"F0.wireOp",EDGE,"E6"),sQuery(id+"F0.wireOp",EDGE,"E7"),sQuery(id+"F0.wireOp",EDGE,"E8"),sQuery(id+"F0.wireOp",EDGE,"E9"),sQuery(id+"F0.wireOp",EDGE,"E10"),sQuery(id+"F0.wireOp",EDGE,"E11"),sQuery(id+"F0.wireOp",EDGE,"E12"),sQuery(id+"F0.wireOp",EDGE,"E13"),sQuery(id+"F0.wireOp",EDGE,"E14"),sQuery(id+"F0.wireOp",EDGE,"E15"),sQuery(id+"F0.wireOp",EDGE,"E16"),sQuery(id+"F0.wireOp",EDGE,"E17"),sQuery(id+"F0.wireOp",EDGE,"E18"),sQuery(id+"F0.wireOp",EDGE,"E19"),sQuery(id+"F0.wireOp",EDGE,"E20"),sQuery(id+"F0.wireOp",EDGE,"E21"),sQuery(id+"F0.wireOp",EDGE,"E22"),sQuery(id+"F0.wireOp",EDGE,"E23"),sQuery(id+"F0.wireOp",EDGE,"E24"),sQuery(id+"F0.wireOp",EDGE,"E25"),sQuery(id+"F0.wireOp",EDGE,"E26"),sQuery(id+"F0.wireOp",EDGE,"E27"),sQuery(id+"F0.wireOp",EDGE,"E28"),sQuery(id+"F0.wireOp",EDGE,"E29"),sQuery(id+"F0.wireOp",EDGE,"E30"),sQuery(id+"F0.wireOp",EDGE,"E31"),sQuery(id+"F0.wireOp",EDGE,"E32"),sQuery(id+"F0.wireOp",EDGE,"E33"),sQuery(id+"F0.wireOp",EDGE,"E34"),sQuery(id+"F0.wireOp",EDGE,"E35"),sQuery(id+"F0.wireOp",EDGE,"E36"),sQuery(id+"F0.wireOp",EDGE,"E37"),sQuery(id+"F0.wireOp",EDGE,"E38"),sQuery(id+"F0.wireOp",EDGE,"E39"),sQuery(id+"F0.wireOp",EDGE,"E40"),sQuery(id+"F0.wireOp",EDGE,"E41"),sQuery(id+"F0.wireOp",EDGE,"E42"),sQuery(id+"F0.wireOp",EDGE,"E43"),sQuery(id+"F0.wireOp",EDGE,"E44"),sQuery(id+"F0.wireOp",EDGE,"E45"),sQuery(id+"F0.wireOp",EDGE,"E46"),sQuery(id+"F0.wireOp",EDGE,"E47"),sQuery(id+"F0.wireOp",EDGE,"E48"),sQuery(id+"F0.wireOp",EDGE,"E49"),sQuery(id+"F0.wireOp",EDGE,"E50")])],"isStart":true}),makeQuery(id+"F3.opExtrude","SWEPT_FACE",FACE,{"disambiguationData":[OSD([sQuery(id+"F2.wireOp",EDGE,"E75")])]})]});
            var Q10;
            Q10=makeQuery(id+"F3.boolean.opBoolean","INTERSECT",EDGE,{"derivedFrom":[makeQuery(id+"F1.opExtrude","CAP_FACE",FACE,{"disambiguationData":[OSD([sQuery(id+"F0.wireOp",EDGE,"E0"),sQuery(id+"F0.wireOp",EDGE,"E1"),sQuery(id+"F0.wireOp",EDGE,"E2"),sQuery(id+"F0.wireOp",EDGE,"E3"),sQuery(id+"F0.wireOp",EDGE,"E4"),sQuery(id+"F0.wireOp",EDGE,"E5"),sQuery(id+"F0.wireOp",EDGE,"E6"),sQuery(id+"F0.wireOp",EDGE,"E7"),sQuery(id+"F0.wireOp",EDGE,"E8"),sQuery(id+"F0.wireOp",EDGE,"E9"),sQuery(id+"F0.wireOp",EDGE,"E10"),sQuery(id+"F0.wireOp",EDGE,"E11"),sQuery(id+"F0.wireOp",EDGE,"E12"),sQuery(id+"F0.wireOp",EDGE,"E13"),sQuery(id+"F0.wireOp",EDGE,"E14"),sQuery(id+"F0.wireOp",EDGE,"E15"),sQuery(id+"F0.wireOp",EDGE,"E16"),sQuery(id+"F0.wireOp",EDGE,"E17"),sQuery(id+"F0.wireOp",EDGE,"E18"),sQuery(id+"F0.wireOp",EDGE,"E19"),sQuery(id+"F0.wireOp",EDGE,"E20"),sQuery(id+"F0.wireOp",EDGE,"E21"),sQuery(id+"F0.wireOp",EDGE,"E22"),sQuery(id+"F0.wireOp",EDGE,"E23"),sQuery(id+"F0.wireOp",EDGE,"E24"),sQuery(id+"F0.wireOp",EDGE,"E25"),sQuery(id+"F0.wireOp",EDGE,"E26"),sQuery(id+"F0.wireOp",EDGE,"E27"),sQuery(id+"F0.wireOp",EDGE,"E28"),sQuery(id+"F0.wireOp",EDGE,"E29"),sQuery(id+"F0.wireOp",EDGE,"E30"),sQuery(id+"F0.wireOp",EDGE,"E31"),sQuery(id+"F0.wireOp",EDGE,"E32"),sQuery(id+"F0.wireOp",EDGE,"E33"),sQuery(id+"F0.wireOp",EDGE,"E34"),sQuery(id+"F0.wireOp",EDGE,"E35"),sQuery(id+"F0.wireOp",EDGE,"E36"),sQuery(id+"F0.wireOp",EDGE,"E37"),sQuery(id+"F0.wireOp",EDGE,"E38"),sQuery(id+"F0.wireOp",EDGE,"E39"),sQuery(id+"F0.wireOp",EDGE,"E40"),sQuery(id+"F0.wireOp",EDGE,"E41"),sQuery(id+"F0.wireOp",EDGE,"E42"),sQuery(id+"F0.wireOp",EDGE,"E43"),sQuery(id+"F0.wireOp",EDGE,"E44"),sQuery(id+"F0.wireOp",EDGE,"E45"),sQuery(id+"F0.wireOp",EDGE,"E46"),sQuery(id+"F0.wireOp",EDGE,"E47"),sQuery(id+"F0.wireOp",EDGE,"E48"),sQuery(id+"F0.wireOp",EDGE,"E49"),sQuery(id+"F0.wireOp",EDGE,"E50")])],"isStart":true}),makeQuery(id+"F3.opExtrude","SWEPT_FACE",FACE,{"disambiguationData":[OSD([sQuery(id+"F2.wireOp",EDGE,"E73")])]})]});
            var Q11;
            Q11=makeQuery(id+"F3.boolean.opBoolean","INTERSECT",EDGE,{"derivedFrom":[makeQuery(id+"F1.opExtrude","CAP_FACE",FACE,{"disambiguationData":[OSD([sQuery(id+"F0.wireOp",EDGE,"E0"),sQuery(id+"F0.wireOp",EDGE,"E1"),sQuery(id+"F0.wireOp",EDGE,"E2"),sQuery(id+"F0.wireOp",EDGE,"E3"),sQuery(id+"F0.wireOp",EDGE,"E4"),sQuery(id+"F0.wireOp",EDGE,"E5"),sQuery(id+"F0.wireOp",EDGE,"E6"),sQuery(id+"F0.wireOp",EDGE,"E7"),sQuery(id+"F0.wireOp",EDGE,"E8"),sQuery(id+"F0.wireOp",EDGE,"E9"),sQuery(id+"F0.wireOp",EDGE,"E10"),sQuery(id+"F0.wireOp",EDGE,"E11"),sQuery(id+"F0.wireOp",EDGE,"E12"),sQuery(id+"F0.wireOp",EDGE,"E13"),sQuery(id+"F0.wireOp",EDGE,"E14"),sQuery(id+"F0.wireOp",EDGE,"E15"),sQuery(id+"F0.wireOp",EDGE,"E16"),sQuery(id+"F0.wireOp",EDGE,"E17"),sQuery(id+"F0.wireOp",EDGE,"E18"),sQuery(id+"F0.wireOp",EDGE,"E19"),sQuery(id+"F0.wireOp",EDGE,"E20"),sQuery(id+"F0.wireOp",EDGE,"E21"),sQuery(id+"F0.wireOp",EDGE,"E22"),sQuery(id+"F0.wireOp",EDGE,"E23"),sQuery(id+"F0.wireOp",EDGE,"E24"),sQuery(id+"F0.wireOp",EDGE,"E25"),sQuery(id+"F0.wireOp",EDGE,"E26"),sQuery(id+"F0.wireOp",EDGE,"E27"),sQuery(id+"F0.wireOp",EDGE,"E28"),sQuery(id+"F0.wireOp",EDGE,"E29"),sQuery(id+"F0.wireOp",EDGE,"E30"),sQuery(id+"F0.wireOp",EDGE,"E31"),sQuery(id+"F0.wireOp",EDGE,"E32"),sQuery(id+"F0.wireOp",EDGE,"E33"),sQuery(id+"F0.wireOp",EDGE,"E34"),sQuery(id+"F0.wireOp",EDGE,"E35"),sQuery(id+"F0.wireOp",EDGE,"E36"),sQuery(id+"F0.wireOp",EDGE,"E37"),sQuery(id+"F0.wireOp",EDGE,"E38"),sQuery(id+"F0.wireOp",EDGE,"E39"),sQuery(id+"F0.wireOp",EDGE,"E40"),sQuery(id+"F0.wireOp",EDGE,"E41"),sQuery(id+"F0.wireOp",EDGE,"E42"),sQuery(id+"F0.wireOp",EDGE,"E43"),sQuery(id+"F0.wireOp",EDGE,"E44"),sQuery(id+"F0.wireOp",EDGE,"E45"),sQuery(id+"F0.wireOp",EDGE,"E46"),sQuery(id+"F0.wireOp",EDGE,"E47"),sQuery(id+"F0.wireOp",EDGE,"E48"),sQuery(id+"F0.wireOp",EDGE,"E49"),sQuery(id+"F0.wireOp",EDGE,"E50")])],"isStart":true}),makeQuery(id+"F3.opExtrude","SWEPT_FACE",FACE,{"disambiguationData":[OSD([sQuery(id+"F2.wireOp",EDGE,"E71")])]})]});
            fillet(context, id + "F4", {"entities" : qUnion([Q0, Q1, Q2, Q3, Q4, Q5, Q6, Q7, Q8, Q9, Q10, Q11]), "tangentPropagation" : true, "radius" : 1.5 * mm, "defaultsChanged" : false, "vertexSettings" : [], "allowEdgeOverflow" : false});
        }
        {
            var Q0;
            Q0=makeQuery(id+"F1.opExtrude","CAP_EDGE",EDGE,{"disambiguationData":[OSD([sQuery(id+"F0.wireOp",EDGE,"E49")])],"isStart":false});
            var Q1;
            Q1=makeQuery(id+"F1.opExtrude","CAP_EDGE",EDGE,{"disambiguationData":[OSD([sQuery(id+"F0.wireOp",EDGE,"E29")])],"isStart":false});
            var Q2;
            Q2=makeQuery(id+"F1.opExtrude","CAP_EDGE",EDGE,{"disambiguationData":[OSD([sQuery(id+"F0.wireOp",EDGE,"E30")])],"isStart":false});
            var Q3;
            Q3=makeQuery(id+"F1.opExtrude","CAP_EDGE",EDGE,{"disambiguationData":[OSD([sQuery(id+"F0.wireOp",EDGE,"E31")])],"isStart":false});
            var Q4;
            Q4=makeQuery(id+"F1.opExtrude","CAP_EDGE",EDGE,{"disambiguationData":[OSD([sQuery(id+"F0.wireOp",EDGE,"E32")])],"isStart":false});
            var Q5;
            Q5=makeQuery(id+"F1.opExtrude","CAP_EDGE",EDGE,{"disambiguationData":[OSD([sQuery(id+"F0.wireOp",EDGE,"E34")])],"isStart":false});
            var Q6;
            Q6=makeQuery(id+"F1.opExtrude","CAP_EDGE",EDGE,{"disambiguationData":[OSD([sQuery(id+"F0.wireOp",EDGE,"E36")])],"isStart":false});
            var Q7;
            Q7=makeQuery(id+"F1.opExtrude","CAP_EDGE",EDGE,{"disambiguationData":[OSD([sQuery(id+"F0.wireOp",EDGE,"E37")])],"isStart":false});
            var Q8;
            Q8=makeQuery(id+"F1.opExtrude","CAP_EDGE",EDGE,{"disambiguationData":[OSD([sQuery(id+"F0.wireOp",EDGE,"E38")])],"isStart":false});
            var Q9;
            Q9=makeQuery(id+"F1.opExtrude","CAP_EDGE",EDGE,{"disambiguationData":[OSD([sQuery(id+"F0.wireOp",EDGE,"E43")])],"isStart":false});
            var Q10;
            Q10=makeQuery(id+"F1.opExtrude","CAP_EDGE",EDGE,{"disambiguationData":[OSD([sQuery(id+"F0.wireOp",EDGE,"E45")])],"isStart":false});
            var Q11;
            Q11=makeQuery(id+"F1.opExtrude","CAP_EDGE",EDGE,{"disambiguationData":[OSD([sQuery(id+"F0.wireOp",EDGE,"E47")])],"isStart":false});
            fillet(context, id + "F5", {"entities" : qUnion([Q0, Q1, Q2, Q3, Q4, Q5, Q6, Q7, Q8, Q9, Q10, Q11]), "tangentPropagation" : true, "radius" : 1.5 * mm, "defaultsChanged" : true, "vertexSettings" : [], "allowEdgeOverflow" : false});
        }
    });
